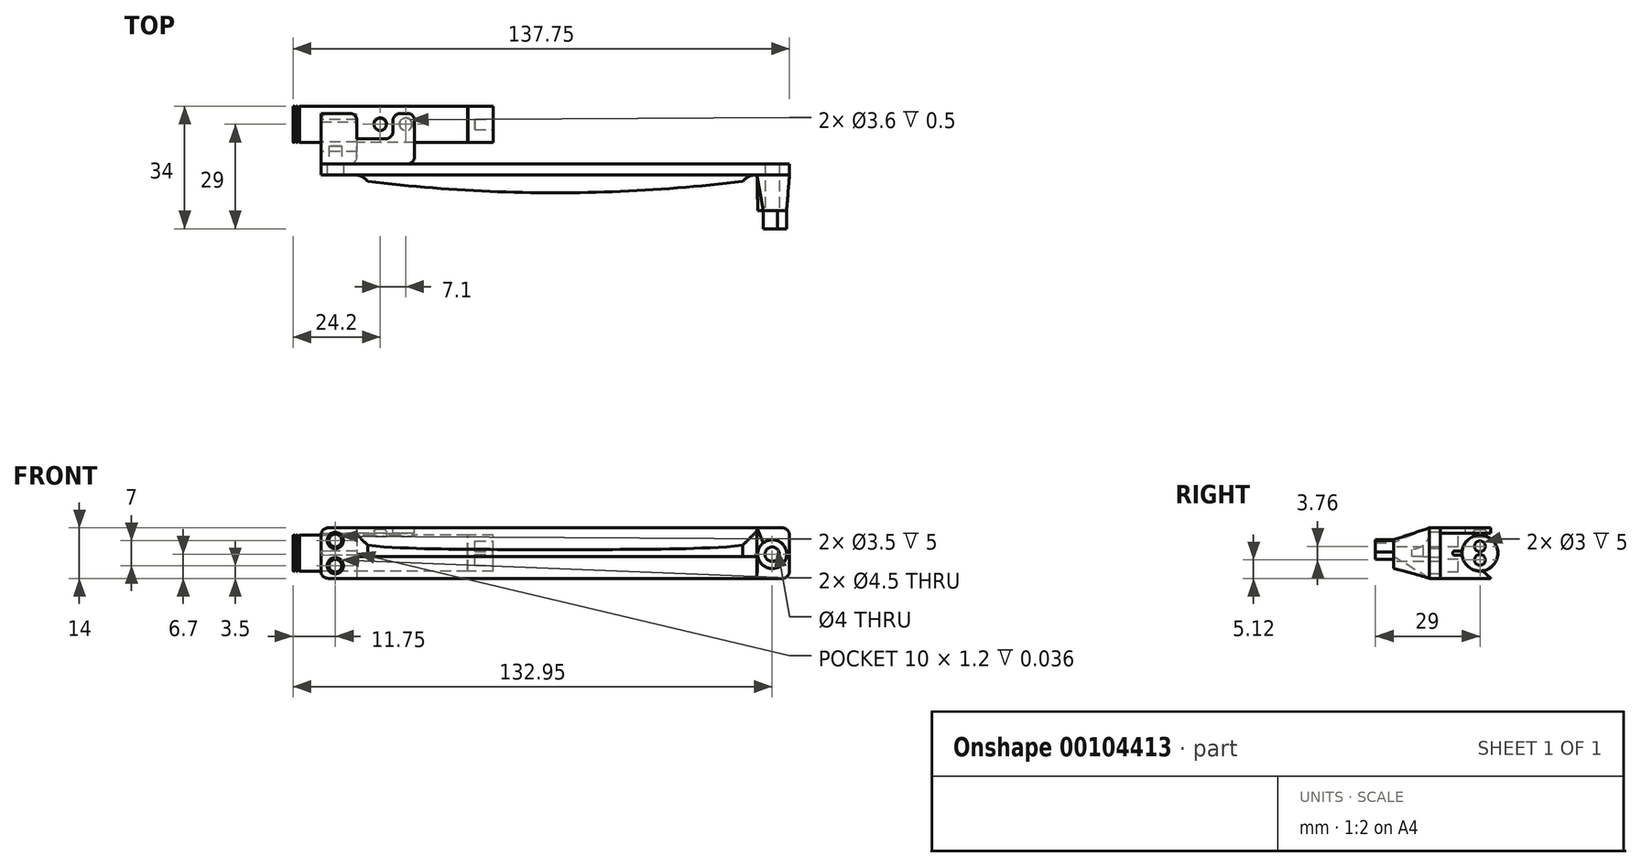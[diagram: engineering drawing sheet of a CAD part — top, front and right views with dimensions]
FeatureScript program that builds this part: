
annotation { "Feature Type Name" : "Feature", "Feature Type Description" : "" }
export const myFeature = defineFeature(function(context is Context, id is Id, definition is map)
    precondition{}
    {
        {
            var Q0;
            Q0=qCreatedBy(makeId("Right.planeOp"),FACE);
            var sketch = newSketch(context, id + "F0", { "sketchPlane" : qUnion([Q0])});
            skCircle(sketch, "E0", {"center": v(0, 0) * mm, "radius": 5 * mm});
            skSolve(sketch);
        }
        {
            var Q0;
            Q0 = qSketchRegion(id + "F0", true);
            extrude(context, id + "F1", {"entities" : qUnion([Q0]), "endBound" : BoundingType.SYMMETRIC, "depth" : 55.5 * mm});
        }
        {
            var Q0;
            Q0=makeQuery(id+"F1.opExtrude","CAP_FACE",FACE,{"disambiguationData":[OSD([sQuery(id+"F0.wireOp",EDGE,"E0")])],"isStart":false});
            var sketch = newSketch(context, id + "F2", { "sketchPlane" : qUnion([Q0])});
            skPoint(sketch, "E1", {"position": v(0, 5) * mm});
            skLineSegment(sketch, "E2", {"start": v(0, 0) * mm, "end": v(0, 5) * mm});
            skSolve(sketch);
        }
        {
            var Q0;
            Q0=qCreatedBy(makeId("Front.planeOp"),FACE);
            var sketch = newSketch(context, id + "F3", { "sketchPlane" : qUnion([Q0])});
            skLineSegment(sketch, "E3.bottom", {"start": v(20.65, 5) * mm, "end": v(20.75, 5) * mm});
            skLineSegment(sketch, "E3.top", {"start": v(20.65, 4.8) * mm, "end": v(20.75, 4.8) * mm});
            skLineSegment(sketch, "E3.left", {"start": v(20.65, 5) * mm, "end": v(20.65, 4.8) * mm});
            skLineSegment(sketch, "E3.right", {"start": v(20.75, 5) * mm, "end": v(20.75, 4.8) * mm});
            skSolve(sketch);
        }
        {
            var Q0;
            Q0 = qSketchRegion(id + "F3", true);
            var Q1;
            Q1=makeQuery(id+"F1.opExtrude","CAP_EDGE",EDGE,{"disambiguationData":[OSD([sQuery(id+"F0.wireOp",EDGE,"E0")])],"isStart":false});
            revolve(context, id + "F4", {"operationType" : NewBodyOperationType.REMOVE, "entities" : qUnion([Q0]), "axis" : qUnion([Q1]), "revolveType" : RevolveType.FULL, "oppositeDirection" : true});
        }
        {
            var Q0;
            Q0=qCreatedBy(makeId("Front.planeOp"),FACE);
            var sketch = newSketch(context, id + "F5", { "sketchPlane" : qUnion([Q0])});
            skArc(sketch, "E4", {"start": v(-26.42, 4.88) * mm, "mid": v(-26.14, 4.76) * mm, "end": v(-25.95, 5) * mm});
            skArc(sketch, "E5", {"start": v(-27.32, 5) * mm, "mid": v(-27.32, 5) * mm, "end": v(-27.32, 5) * mm});
            skArc(sketch, "E6", {"start": v(-26.38, 4.74) * mm, "mid": v(-26.38, 4.75) * mm, "end": v(-26.38, 4.75) * mm});
            skLineSegment(sketch, "E7", {"start": v(-27.07, 5) * mm, "end": v(-26.2, 5) * mm, "construction": true});
            skLineSegment(sketch, "E8", {"start": v(-26.87, 4.66) * mm, "end": v(-26.4, 4.66) * mm, "construction": true});
            skLineSegment(sketch, "E9", {"start": v(-27.07, 5) * mm, "end": v(-27.07, 5.56) * mm, "construction": true});
            skArc(sketch, "E10.MirrorCS", {"start": v(-27.75, 4.75) * mm, "mid": v(-27.56, 5) * mm, "end": v(-27.28, 4.87) * mm});
            skLineSegment(sketch, "E11.MirrorCS", {"start": v(-27.75, 4.75) * mm, "end": v(-27.75, 5) * mm});
            skPoint(sketch, "E12.orphan", {"position": v(-27.25, 5.35) * mm});
            skPoint(sketch, "E13.orphan", {"position": v(-26.88, 5.35) * mm});
            skPoint(sketch, "E14.orphan", {"position": v(-26.38, 5.32) * mm});
            skPoint(sketch, "E15.orphan", {"position": v(-27.25, 4.6) * mm});
            skPoint(sketch, "E16.orphan", {"position": v(-27.27, 4.66) * mm});
            skPoint(sketch, "E17.orphan", {"position": v(-27.73, 4.66) * mm});
            skPoint(sketch, "E18.orphan", {"position": v(-26.88, 4.6) * mm});
            skLineSegment(sketch, "E19", {"start": v(-25.95, 5.27) * mm, "end": v(-25.95, 4.5) * mm, "construction": true});
            skLineSegment(sketch, "E20", {"start": v(-25.95, 5) * mm, "end": v(-26.45, 5) * mm});
            skLineSegment(sketch, "E21", {"start": v(-26.45, 5) * mm, "end": v(-27.75, 5) * mm});
            skPoint(sketch, "E22.orphan", {"position": v(-27.75, 5.32) * mm});
            skPoint(sketch, "E23.orphan", {"position": v(-26.38, 4.67) * mm});
            skArc(sketch, "E24.trimOffspring", {"start": v(-27.28, 4.87) * mm, "mid": v(-27.07, 4.75) * mm, "end": v(-26.85, 4.87) * mm});
            skArc(sketch, "E25.trimOffspring", {"start": v(-27.25, 4.75) * mm, "mid": v(-27.25, 4.75) * mm, "end": v(-27.25, 4.74) * mm});
            skArc(sketch, "E26.trimOffspring", {"start": v(-26.88, 4.75) * mm, "mid": v(-26.88, 4.75) * mm, "end": v(-26.88, 4.74) * mm});
            skArc(sketch, "E27.trimOffspring", {"start": v(-26.42, 4.88) * mm, "mid": v(-26.63, 5) * mm, "end": v(-26.85, 4.87) * mm});
            skPoint(sketch, "E28.orphan", {"position": v(-27.75, 4.67) * mm});
            skSolve(sketch);
        }
        {
            var Q0;
            Q0 = qSketchRegion(id + "F5", true);
            var Q1;
            {var subQ0=sQuery(id+"F0.wireOp",EDGE,"E0");Q1=makeQuery(id+"F4.boolean.opBoolean","SPLIT",FACE,{"disambiguationData":[TD([makeQuery(id+"F1.opExtrude","CAP_FACE",FACE,{"disambiguationData":[OSD([subQ0])],"isStart":true})])],"derivedFrom":makeQuery(id+"F1.opExtrude","SWEPT_FACE",FACE,{"disambiguationData":[OSD([subQ0])]})});}
            revolve(context, id + "F6", {"operationType" : NewBodyOperationType.REMOVE, "entities" : qUnion([Q0]), "axis" : qUnion([Q1]), "revolveType" : RevolveType.FULL, "oppositeDirection" : true});
        }
        {
            var Q0;
            Q0=makeQuery(id+"F1.opExtrude","CAP_FACE",FACE,{"disambiguationData":[OSD([sQuery(id+"F0.wireOp",EDGE,"E0")])],"isStart":false});
            var sketch = newSketch(context, id + "F7", { "sketchPlane" : qUnion([Q0])});
            skCircle(sketch, "E29", {"center": v(0, 1.88) * mm, "radius": 1.5 * mm});
            skCircle(sketch, "E30", {"center": v(0, -1.88) * mm, "radius": 1.5 * mm});
            skLineSegment(sketch, "E31", {"start": v(0, 1.88) * mm, "end": v(0, 0) * mm, "construction": true});
            skLineSegment(sketch, "E32", {"start": v(0, 0) * mm, "end": v(0, -1.88) * mm, "construction": true});
            skSolve(sketch);
        }
        {
            var Q0;
            Q0 = qSketchRegion(id + "F7", true);
            extrude(context, id + "F8", {"entities" : qUnion([Q0]), "operationType" : NewBodyOperationType.REMOVE, "oppositeDirection" : true, "depth" : 5 * mm});
        }
        {
            var Q0;
            Q0=sQuery(id+"F2.wireOp",VERTEX,"E1");
            var Q1;
            Q1=qCreatedBy(makeId("Top.planeOp"),FACE);
            cPlane(context, id + "F9", {"entities" : qUnion([Q0, Q1]), "cplaneType" : CPlaneType.PLANE_POINT, "offset" : 150 * mm, "width" : 150 * mm, "height" : 150 * mm});
        }
        {
            var Q0;
            Q0=qCreatedBy(id+"F9.planeOp",FACE);
            var sketch = newSketch(context, id + "F10", { "sketchPlane" : qUnion([Q0])});
            skCircle(sketch, "E33", {"center": v(-3.55, 0) * mm, "radius": 1.7 * mm});
            skCircle(sketch, "E34", {"center": v(3.55, 0) * mm, "radius": 1.7 * mm});
            skSolve(sketch);
        }
        {
            var Q0;
            Q0 = qSketchRegion(id + "F10", true);
            var Q1;
            {var subQ0=sQuery(id+"F0.wireOp",EDGE,"E0");Q1=makeQuery(id+"F4.boolean.opBoolean","SPLIT",FACE,{"disambiguationData":[TD([makeQuery(id+"F1.opExtrude","CAP_FACE",FACE,{"disambiguationData":[OSD([subQ0])],"isStart":true})])],"derivedFrom":makeQuery(id+"F1.opExtrude","SWEPT_FACE",FACE,{"disambiguationData":[OSD([subQ0])]})});}
            extrude(context, id + "F11", {"entities" : qUnion([Q0]), "operationType" : NewBodyOperationType.ADD, "depth" : 1.5 * mm, "hasSecondDirection" : true, "secondDirectionBound" : SecondDirectionBoundingType.UP_TO_SURFACE, "secondDirectionOppositeDirection" : true, "secondDirectionBoundEntityFace" : qUnion([Q1]), "secondDirectionDepth" : 25 * mm});
        }
        {
            var Q0;
            Q0=makeQuery(id+"F11.opExtrude","CAP_EDGE",EDGE,{"disambiguationData":[OSD([sQuery(id+"F10.wireOp",EDGE,"E33")]),OD(1.0)],"isStart":false});
            var Q1;
            Q1=makeQuery(id+"F11.opExtrude","CAP_EDGE",EDGE,{"disambiguationData":[OSD([sQuery(id+"F10.wireOp",EDGE,"E34")]),OD(1.0)],"isStart":false});
            fillet(context, id + "F12", {"entities" : qUnion([Q0, Q1]), "radius" : .5 * mm, "tangentPropagation" : true, "allowEdgeOverflow" : false});
        }
        {
            var Q0;
            Q0=qCreatedBy(id+"F9.planeOp",FACE);
            var sketch = newSketch(context, id + "F13", { "sketchPlane" : qUnion([Q0])});
            skCircle(sketch, "E35.0", {"center": v(-3.55, 0) * mm, "radius": 1.7 * mm});
            skCircle(sketch, "E35.1", {"center": v(3.55, 0) * mm, "radius": 1.7 * mm});
            skCircle(sketch, "E36.0", {"center": v(-3.55, 0) * mm, "radius": 1.8 * mm});
            skCircle(sketch, "E37.0", {"center": v(3.55, 0) * mm, "radius": 1.8 * mm});
            skSolve(sketch);
        }
        {
            var Q0;
            Q0 = qSketchRegion(id + "F13", true);
            extrude(context, id + "F14", {"entities" : qUnion([Q0]), "operationType" : NewBodyOperationType.REMOVE, "oppositeDirection" : true, "depth" : .5 * mm});
        }
        {
            var Q0;
            Q0=qCreatedBy(makeId("Right.planeOp"),FACE);
            cPlane(context, id + "F15", {"entities" : qUnion([Q0]), "cplaneType" : CPlaneType.OFFSET, "offset" : 10 * mm, "oppositeDirection" : true, "width" : 150 * mm, "height" : 150 * mm});
        }
        {
            var Q0;
            Q0=qCreatedBy(id+"F15.planeOp",FACE);
            var sketch = newSketch(context, id + "F16", { "sketchPlane" : qUnion([Q0])});
            skArc(sketch, "E38.0", {"start": v(3, 4) * mm, "mid": v(-5, 0) * mm, "end": v(3, -4) * mm});
            skLineSegment(sketch, "E39", {"start": v(3, 7) * mm, "end": v(3, 4) * mm});
            skLineSegment(sketch, "E40", {"start": v(0, 0) * mm, "end": v(3, 0) * mm});
            skLineSegment(sketch, "E41", {"start": v(3, 7) * mm, "end": v(-11, 7) * mm});
            skLineSegment(sketch, "E42", {"start": v(-11, 7) * mm, "end": v(-11, -7) * mm});
            skLineSegment(sketch, "E43", {"start": v(-11, -7) * mm, "end": v(3, -7) * mm});
            skLineSegment(sketch, "E44.trimOffspring", {"start": v(3, -4) * mm, "end": v(3, -7) * mm});
            skSolve(sketch);
        }
        {
            var Q0;
            Q0 = qSketchRegion(id + "F16", true);
            extrude(context, id + "F17", {"entities" : qUnion([Q0]), "oppositeDirection" : true, "depth" : 10 * mm});
        }
        {
            var Q0;
            Q0=makeQuery(id+"F17.opExtrude","SWEPT_EDGE",EDGE,{"disambiguationData":[OSD([sQuery(id+"F16.wireOp",EDGE,"E38.0"),sQuery(id+"F16.wireOp",EDGE,"E39")])]});
            var Q1;
            Q1=makeQuery(id+"F17.opExtrude","SWEPT_EDGE",EDGE,{"disambiguationData":[OSD([sQuery(id+"F16.wireOp",EDGE,"E38.0"),sQuery(id+"F16.wireOp",EDGE,"E44.trimOffspring")])]});
            chamfer(context, id + "F18", {"entities" : qUnion([Q0, Q1]), "width" : 2 * mm, "tangentPropagation" : true});
        }
        {
            var Q0;
            Q0=makeQuery(id+"F17.opExtrude","SWEPT_FACE",FACE,{"disambiguationData":[OSD([sQuery(id+"F16.wireOp",EDGE,"E41")])]});
            var sketch = newSketch(context, id + "F19", { "sketchPlane" : qUnion([Q0])});
            skLineSegment(sketch, "E45.bottom", {"start": v(0, 3) * mm, "end": v(6, 3) * mm});
            skLineSegment(sketch, "E45.top", {"start": v(-20, -11) * mm, "end": v(6, -11) * mm});
            skLineSegment(sketch, "E45.left", {"start": v(-20, 3) * mm, "end": v(-20, -11) * mm});
            skLineSegment(sketch, "E45.right", {"start": v(6, 3) * mm, "end": v(6, -11) * mm});
            skLineSegment(sketch, "E46", {"start": v(0, 3) * mm, "end": v(0, -4) * mm});
            skLineSegment(sketch, "E47", {"start": v(0, -4) * mm, "end": v(-10, -4) * mm});
            skLineSegment(sketch, "E48", {"start": v(-10, -4) * mm, "end": v(-10, 3) * mm});
            skLineSegment(sketch, "E49", {"start": v(-10, 3) * mm, "end": v(-20, 3) * mm});
            skSolve(sketch);
        }
        {
            var Q0;
            Q0 = qSketchRegion(id + "F19", true);
            extrude(context, id + "F20", {"entities" : qUnion([Q0]), "operationType" : NewBodyOperationType.ADD, "oppositeDirection" : true, "depth" : 1.5 * mm});
        }
        {
            var Q0;
            Q0=makeQuery(id+"F20.opExtrude","SWEPT_EDGE",EDGE,{"disambiguationData":[OSD([sQuery(id+"F19.wireOp",EDGE,"E46"),sQuery(id+"F19.wireOp",EDGE,"E47")])]});
            var Q1;
            Q1=makeQuery(id+"F20.opExtrude","SWEPT_EDGE",EDGE,{"disambiguationData":[OSD([sQuery(id+"F16.wireOp",EDGE,"E41"),sQuery(id+"F19.wireOp",EDGE,"E47"),sQuery(id+"F19.wireOp",EDGE,"E48")])]});
            var Q2;
            Q2=makeQuery(id+"F20.boolean.opBoolean","MERGE",EDGE,{"derivedFrom":[makeQuery(id+"F17.opExtrude","CAP_EDGE",EDGE,{"disambiguationData":[OSD([sQuery(id+"F16.wireOp",EDGE,"E39")])],"isStart":true}),makeQuery(id+"F20.opExtrude","SWEPT_EDGE",EDGE,{"disambiguationData":[OSD([sQuery(id+"F19.wireOp",EDGE,"E48"),sQuery(id+"F19.wireOp",EDGE,"E49")])]})]});
            var Q3;
            Q3=makeQuery(id+"F20.opExtrude","SWEPT_EDGE",EDGE,{"disambiguationData":[OSD([sQuery(id+"F19.wireOp",EDGE,"E45.bottom"),sQuery(id+"F19.wireOp",EDGE,"E46")])]});
            var Q4;
            Q4=makeQuery(id+"F17.opExtrude","CAP_EDGE",EDGE,{"disambiguationData":[OSD([sQuery(id+"F16.wireOp",EDGE,"E42")])],"isStart":true});
            var Q5;
            Q5=makeQuery(id+"F20.opExtrude","SWEPT_EDGE",EDGE,{"disambiguationData":[OSD([sQuery(id+"F19.wireOp",EDGE,"E45.top"),sQuery(id+"F19.wireOp",EDGE,"E45.right")])]});
            var Q6;
            Q6=makeQuery(id+"F20.opExtrude","SWEPT_EDGE",EDGE,{"disambiguationData":[OSD([sQuery(id+"F19.wireOp",EDGE,"E45.bottom"),sQuery(id+"F19.wireOp",EDGE,"E45.right")])]});
            fillet(context, id + "F21", {"entities" : qUnion([Q0, Q1, Q2, Q3, Q4, Q5, Q6]), "radius" : 2 * mm, "tangentPropagation" : true, "allowEdgeOverflow" : false});
        }
        {
            var Q0;
            Q0=makeQuery(id+"F20.boolean.opBoolean","MERGE",FACE,{"derivedFrom":[makeQuery(id+"F17.opExtrude","CAP_FACE",FACE,{"disambiguationData":[OSD([sQuery(id+"F16.wireOp",EDGE,"E38.0"),sQuery(id+"F16.wireOp",EDGE,"E39"),sQuery(id+"F16.wireOp",EDGE,"E41"),sQuery(id+"F16.wireOp",EDGE,"E42"),sQuery(id+"F16.wireOp",EDGE,"E43"),sQuery(id+"F16.wireOp",EDGE,"E44.trimOffspring")])],"isStart":false}),makeQuery(id+"F20.opExtrude","SWEPT_FACE",FACE,{"disambiguationData":[OSD([sQuery(id+"F19.wireOp",EDGE,"E45.left")])]})]});
            var sketch = newSketch(context, id + "F22", { "sketchPlane" : qUnion([Q0])});
            skLineSegment(sketch, "E50", {"start": v(6.96, 0.6) * mm, "end": v(4.96, 0.6) * mm});
            skLineSegment(sketch, "E51", {"start": v(4.96, 0.6) * mm, "end": v(4.96, -0.6) * mm});
            skLineSegment(sketch, "E52", {"start": v(4.96, -0.6) * mm, "end": v(6.96, -0.6) * mm});
            skLineSegment(sketch, "E53", {"start": v(0, 0) * mm, "end": v(9, 0) * mm, "construction": true});
            skArc(sketch, "E54", {"start": v(6.96, -0.6) * mm, "mid": v(7.56, 0) * mm, "end": v(6.96, 0.6) * mm});
            skSolve(sketch);
        }
        {
            var Q0;
            {var subQ0=sQuery(id+"F22.wireOp",EDGE,"yF9MeYyX-MxWM-4ZoS-nlc9-Eh6hePXLtj0A");Q0=makeQuery(id+"F22.imprint","IMPRINT",FACE,{"disambiguationData":[TD([[makeQuery(id+"F22.imprint","IMPRINT",EDGE,{"derivedFrom":subQ0}),1.0]])]});}
            var Q1;
            {var subQ0=sQuery(id+"F22.wireOp",EDGE,"E50");Q1=makeQuery(id+"F22.imprint","IMPRINT",FACE,{"disambiguationData":[TD([[makeQuery(id+"F22.imprint","IMPRINT",EDGE,{"derivedFrom":subQ0}),1.0]])]});}
            var Q2;
            Q2=makeQuery(id+"F20.boolean.opBoolean","MERGE",FACE,{"derivedFrom":[makeQuery(id+"F17.opExtrude","CAP_FACE",FACE,{"disambiguationData":[OSD([sQuery(id+"F16.wireOp",EDGE,"E38.0"),sQuery(id+"F16.wireOp",EDGE,"E39"),sQuery(id+"F16.wireOp",EDGE,"E41"),sQuery(id+"F16.wireOp",EDGE,"E42"),sQuery(id+"F16.wireOp",EDGE,"E43"),sQuery(id+"F16.wireOp",EDGE,"E44.trimOffspring")])],"isStart":true}),makeQuery(id+"F20.opExtrude","SWEPT_FACE",FACE,{"disambiguationData":[OSD([sQuery(id+"F19.wireOp",EDGE,"E48")])]})]});
            extrude(context, id + "F23", {"entities" : qUnion([Q0, Q1]), "operationType" : NewBodyOperationType.REMOVE, "endBound" : BoundingType.UP_TO_SURFACE, "oppositeDirection" : true, "endBoundEntityFace" : qUnion([Q2]), "depth" : 25 * mm});
        }
        {
            var Q0;
            Q0=makeQuery(id+"F20.boolean.opBoolean","MERGE",FACE,{"derivedFrom":[makeQuery(id+"F17.opExtrude","SWEPT_FACE",FACE,{"disambiguationData":[OSD([sQuery(id+"F16.wireOp",EDGE,"E42")])]}),makeQuery(id+"F20.opExtrude","SWEPT_FACE",FACE,{"disambiguationData":[OSD([sQuery(id+"F19.wireOp",EDGE,"E45.top")])]})]});
            var sketch = newSketch(context, id + "F24", { "sketchPlane" : qUnion([Q0])});
            skCircle(sketch, "E55", {"center": v(-16, 3.5) * mm, "radius": 1.75 * mm});
            skCircle(sketch, "E56", {"center": v(-16, -3.5) * mm, "radius": 1.75 * mm});
            skLineSegment(sketch, "E57", {"start": v(-16, 3.5) * mm, "end": v(-16, -3.5) * mm, "construction": true});
            skLineSegment(sketch, "E58", {"start": v(0, 0) * mm, "end": v(-16, 0) * mm, "construction": true});
            skLineSegment(sketch, "E59", {"start": v(-16, -7) * mm, "end": v(-16, -3.5) * mm, "construction": true});
            skSolve(sketch);
        }
        {
            var Q0;
            Q0 = qSketchRegion(id + "F24", true);
            extrude(context, id + "F25", {"entities" : qUnion([Q0]), "operationType" : NewBodyOperationType.REMOVE, "oppositeDirection" : true, "depth" : 5 * mm});
        }
        {
            var Q0;
            Q0=makeQuery(id+"F20.boolean.opBoolean","MERGE",FACE,{"derivedFrom":[makeQuery(id+"F17.opExtrude","SWEPT_FACE",FACE,{"disambiguationData":[OSD([sQuery(id+"F16.wireOp",EDGE,"E42")])]}),makeQuery(id+"F20.opExtrude","SWEPT_FACE",FACE,{"disambiguationData":[OSD([sQuery(id+"F19.wireOp",EDGE,"E45.top")])]})]});
            var sketch = newSketch(context, id + "F26", { "sketchPlane" : qUnion([Q0])});
            skLineSegment(sketch, "E60.bottom", {"start": v(-20, 7) * mm, "end": v(110, 7) * mm});
            skLineSegment(sketch, "E60.top", {"start": v(-20, -7) * mm, "end": v(110, -7) * mm});
            skLineSegment(sketch, "E60.left", {"start": v(-20, 7) * mm, "end": v(-20, -7) * mm});
            skLineSegment(sketch, "E60.right", {"start": v(110, 7) * mm, "end": v(110, -7) * mm});
            skSolve(sketch);
        }
        {
            var Q0;
            Q0 = qSketchRegion(id + "F26", true);
            extrude(context, id + "F27", {"entities" : qUnion([Q0]), "depth" : 3 * mm});
        }
        {
            var Q0;
            Q0=makeQuery(id+"F27.opExtrude","CAP_FACE",FACE,{"disambiguationData":[OSD([sQuery(id+"F26.wireOp",EDGE,"E60.bottom"),sQuery(id+"F26.wireOp",EDGE,"E60.top"),sQuery(id+"F26.wireOp",EDGE,"E60.left"),sQuery(id+"F26.wireOp",EDGE,"E60.right")])],"isStart":false});
            var sketch = newSketch(context, id + "F28", { "sketchPlane" : qUnion([Q0])});
            skPoint(sketch, "E61", {"position": v(-20, 0) * mm});
            skSolve(sketch);
        }
        {
            var Q0;
            Q0=sQuery(id+"F28.wireOp",VERTEX,"E61");
            var Q1;
            Q1=qCreatedBy(makeId("Top.planeOp"),FACE);
            cPlane(context, id + "F29", {"entities" : qUnion([Q0, Q1]), "cplaneType" : CPlaneType.PLANE_POINT, "offset" : 150 * mm, "width" : 150 * mm, "height" : 150 * mm});
        }
        {
            var Q0;
            Q0=qCreatedBy(id+"F29.planeOp",FACE);
            var sketch = newSketch(context, id + "F30", { "sketchPlane" : qUnion([Q0])});
            skArc(sketch, "E62", {"start": v(-20, -14) * mm, "mid": v(45, -19) * mm, "end": v(110, -14) * mm});
            skLineSegment(sketch, "E63", {"start": v(-20, -14) * mm, "end": v(110, -14) * mm});
            skSolve(sketch);
        }
        {
            var Q0;
            Q0 = qSketchRegion(id + "F30", true);
            extrude(context, id + "F31", {"entities" : qUnion([Q0]), "operationType" : NewBodyOperationType.ADD, "endBound" : BoundingType.SYMMETRIC, "depth" : 2 * mm});
        }
        {
            var Q0;
            Q0=makeQuery(id+"F28.imprint","IMPRINT",FACE,{"disambiguationData":[TD([[makeQuery(id+"F28.imprint","IMPRINT",EDGE,{"derivedFrom":makeQuery(id+"F27.opExtrude","CAP_EDGE",EDGE,{"disambiguationData":[OSD([sQuery(id+"F26.wireOp",EDGE,"E60.bottom")])],"isStart":false})}),-1.0]])]});
            var sketch = newSketch(context, id + "F32", { "sketchPlane" : qUnion([Q0])});
            skPoint(sketch, "E64", {"position": v(-16, 3.5) * mm});
            skPoint(sketch, "E65", {"position": v(-16, -3.5) * mm});
            skSolve(sketch);
        }
        {
            var Q0;
            Q0=sQuery(id+"F32.wireOp",VERTEX,"E64");
            var Q1;
            Q1=sQuery(id+"F32.wireOp",VERTEX,"E65");
            var Q2;
            Q2=makeQuery(id+"F27.opExtrude","SWEPT_BODY",BODY,{"disambiguationData":[OSD([sQuery(id+"F26.wireOp",EDGE,"E60.bottom"),sQuery(id+"F26.wireOp",EDGE,"E60.top"),sQuery(id+"F26.wireOp",EDGE,"E60.left"),sQuery(id+"F26.wireOp",EDGE,"E60.right")])]});
            hole(context, id + "F33", {"style" : HoleStyle.SIMPLE, "endStyle" : HoleEndStyle.THROUGH, "holeDiameter" : 4.5 * mm, "locations" : qUnion([Q0, Q1]), "scope" : qUnion([Q2]), "isTappedThrough" : true});
        }
        {
            var Q0;
            Q0=makeQuery(id+"F28.imprint","IMPRINT",FACE,{"disambiguationData":[TD([[makeQuery(id+"F28.imprint","IMPRINT",EDGE,{"derivedFrom":makeQuery(id+"F27.opExtrude","CAP_EDGE",EDGE,{"disambiguationData":[OSD([sQuery(id+"F26.wireOp",EDGE,"E60.bottom")])],"isStart":false})}),-1.0]])]});
            var sketch = newSketch(context, id + "F34", { "sketchPlane" : qUnion([Q0])});
            skPoint(sketch, "E66", {"position": v(45, -7) * mm});
            skSolve(sketch);
        }
        {
            var Q0;
            Q0=qCreatedBy(makeId("Right.planeOp"),FACE);
            var Q1;
            Q1=sQuery(id+"F34.wireOp",VERTEX,"E66");
            cPlane(context, id + "F35", {"entities" : qUnion([Q0, Q1]), "cplaneType" : CPlaneType.PLANE_POINT, "offset" : 150 * mm, "width" : 150 * mm, "height" : 150 * mm});
        }
        {
            var Q0;
            Q0=makeQuery(id+"F31.opExtrude","CAP_FACE",FACE,{"disambiguationData":[OSD([sQuery(id+"F30.wireOp",EDGE,"E62"),sQuery(id+"F30.wireOp",EDGE,"E63")])],"isStart":true});
            var sketch = newSketch(context, id + "F36", { "sketchPlane" : qUnion([Q0])});
            skLineSegment(sketch, "E67.bottom", {"start": v(-20, 19) * mm, "end": v(-7, 19) * mm});
            skLineSegment(sketch, "E67.top", {"start": v(-20, 14) * mm, "end": v(-7, 14) * mm});
            skLineSegment(sketch, "E67.left", {"start": v(-20, 19) * mm, "end": v(-20, 14) * mm});
            skLineSegment(sketch, "E67.right", {"start": v(-7, 19) * mm, "end": v(-7, 14) * mm});
            skLineSegment(sketch, "E68.MirrorCS", {"start": v(110, 19) * mm, "end": v(110, 14) * mm});
            skLineSegment(sketch, "E69.MirrorCS", {"start": v(97, 19) * mm, "end": v(97, 14) * mm});
            skLineSegment(sketch, "E70.MirrorCS", {"start": v(110, 19) * mm, "end": v(97, 19) * mm});
            skLineSegment(sketch, "E71.MirrorCS", {"start": v(110, 14) * mm, "end": v(97, 14) * mm});
            skSolve(sketch);
        }
        {
            var Q0;
            {var subQ0=sQuery(id+"F36.wireOp",EDGE,"E67.top");Q0=makeQuery(id+"F36.imprint","IMPRINT",FACE,{"disambiguationData":[TD([[makeQuery(id+"F36.imprint","IMPRINT",EDGE,{"derivedFrom":subQ0}),1.0]])]});}
            var Q1;
            {var subQ0=sQuery(id+"F36.wireOp",EDGE,"E71.MirrorCS");Q1=makeQuery(id+"F36.imprint","IMPRINT",FACE,{"disambiguationData":[TD([[makeQuery(id+"F36.imprint","IMPRINT",EDGE,{"derivedFrom":subQ0}),1.0]])]});}
            extrude(context, id + "F37", {"entities" : qUnion([Q0, Q1]), "operationType" : NewBodyOperationType.REMOVE, "endBound" : BoundingType.THROUGH_ALL, "oppositeDirection" : true, "depth" : 25 * mm});
        }
        {
            var Q0;
            Q0=makeQuery(id+"F27.opExtrude","SWEPT_EDGE",EDGE,{"disambiguationData":[OSD([sQuery(id+"F26.wireOp",EDGE,"E60.bottom"),sQuery(id+"F26.wireOp",EDGE,"E60.left")])]});
            var Q1;
            Q1=makeQuery(id+"F17.opExtrude","CAP_EDGE",EDGE,{"disambiguationData":[OSD([sQuery(id+"F16.wireOp",EDGE,"E41")])],"isStart":false});
            var Q2;
            Q2=makeQuery(id+"F17.opExtrude","CAP_EDGE",EDGE,{"disambiguationData":[OSD([sQuery(id+"F16.wireOp",EDGE,"E43")])],"isStart":false});
            var Q3;
            Q3=makeQuery(id+"F27.opExtrude","SWEPT_EDGE",EDGE,{"disambiguationData":[OSD([sQuery(id+"F26.wireOp",EDGE,"E60.top"),sQuery(id+"F26.wireOp",EDGE,"E60.left")])]});
            var Q4;
            Q4=makeQuery(id+"F27.opExtrude","SWEPT_EDGE",EDGE,{"disambiguationData":[OSD([sQuery(id+"F26.wireOp",EDGE,"E60.bottom"),sQuery(id+"F26.wireOp",EDGE,"E60.right")])]});
            var Q5;
            Q5=makeQuery(id+"F27.opExtrude","SWEPT_EDGE",EDGE,{"disambiguationData":[OSD([sQuery(id+"F26.wireOp",EDGE,"E60.top"),sQuery(id+"F26.wireOp",EDGE,"E60.right")])]});
            var Q6;
            Q6=makeQuery(id+"F37.boolean.opBoolean","COPY",EDGE,{"derivedFrom":makeQuery(id+"F37.opExtrude","SWEPT_EDGE",EDGE,{"disambiguationData":[OSD([sQuery(id+"F30.wireOp",EDGE,"E62"),sQuery(id+"F36.wireOp",EDGE,"E69.MirrorCS")])]})});
            var Q7;
            Q7=makeQuery(id+"F37.boolean.opBoolean","COPY",EDGE,{"derivedFrom":makeQuery(id+"F37.opExtrude","SWEPT_EDGE",EDGE,{"disambiguationData":[OSD([sQuery(id+"F30.wireOp",EDGE,"E62"),sQuery(id+"F36.wireOp",EDGE,"E67.right")])]})});
            fillet(context, id + "F38", {"entities" : qUnion([Q0, Q1, Q2, Q3, Q4, Q5, Q6, Q7]), "radius" : 2 * mm, "tangentPropagation" : true, "allowEdgeOverflow" : false});
        }
        {
            var Q0;
            Q0=makeQuery(id+"F31.opExtrude","CAP_EDGE",EDGE,{"disambiguationData":[OSD([sQuery(id+"F30.wireOp",EDGE,"E63")])],"isStart":true});
            var Q1;
            Q1=makeQuery(id+"F31.opExtrude","CAP_EDGE",EDGE,{"disambiguationData":[OSD([sQuery(id+"F30.wireOp",EDGE,"E63")])],"isStart":false});
            var Q2;
            Q2=makeQuery(id+"F37.boolean.opBoolean","COPY",EDGE,{"derivedFrom":makeQuery(id+"F37.opExtrude","SWEPT_EDGE",EDGE,{"disambiguationData":[OSD([sQuery(id+"F30.wireOp",EDGE,"E63"),sQuery(id+"F36.wireOp",EDGE,"E69.MirrorCS"),sQuery(id+"F36.wireOp",EDGE,"E71.MirrorCS")])]})});
            var Q3;
            Q3=makeQuery(id+"F37.boolean.opBoolean","COPY",EDGE,{"derivedFrom":makeQuery(id+"F37.opExtrude","SWEPT_EDGE",EDGE,{"disambiguationData":[OSD([sQuery(id+"F30.wireOp",EDGE,"E63"),sQuery(id+"F36.wireOp",EDGE,"E67.top"),sQuery(id+"F36.wireOp",EDGE,"E67.right")])]})});
            fillet(context, id + "F39", {"entities" : qUnion([Q0, Q1, Q2, Q3]), "radius" : 5 * mm, "tangentPropagation" : true, "allowEdgeOverflow" : false});
        }
        {
            var Q0;
            {var subQ2=sQuery(id+"F26.wireOp",EDGE,"E60.top");var subQ3=sQuery(id+"F26.wireOp",EDGE,"E60.right");var subQ5=sQuery(id+"F26.wireOp",EDGE,"E60.left");var subQ8=sQuery(id+"F26.wireOp",EDGE,"E60.bottom");var subQ9=makeQuery(id+"F27.opExtrude","CAP_FACE",FACE,{"disambiguationData":[OSD([subQ8,subQ2,subQ5,subQ3])],"isStart":false});Q0=makeQuery(id+"F37.boolean.opBoolean","MERGE",FACE,{"derivedFrom":[makeQuery(id+"F31.boolean.opBoolean","SPLIT",FACE,{"disambiguationData":[TD([makeQuery(id+"F27.opExtrude","SWEPT_FACE",FACE,{"disambiguationData":[OSD([subQ8])]})])],"derivedFrom":subQ9}),makeQuery(id+"F31.boolean.opBoolean","SPLIT",FACE,{"disambiguationData":[TD([makeQuery(id+"F27.opExtrude","SWEPT_FACE",FACE,{"disambiguationData":[OSD([subQ2])]})])],"derivedFrom":subQ9}),makeQuery(id+"F37.opExtrude","SWEPT_FACE",FACE,{"disambiguationData":[OSD([sQuery(id+"F36.wireOp",EDGE,"E67.top")])]}),makeQuery(id+"F37.opExtrude","SWEPT_FACE",FACE,{"disambiguationData":[OSD([sQuery(id+"F36.wireOp",EDGE,"E71.MirrorCS")])]})]});}
            var sketch = newSketch(context, id + "F40", { "sketchPlane" : qUnion([Q0])});
            skLineSegment(sketch, "E72.0", {"start": v(110, 5) * mm, "end": v(110, -5) * mm});
            skArc(sketch, "E72.1", {"start": v(110, 5) * mm, "mid": v(109.41, 6.41) * mm, "end": v(108, 7) * mm});
            skLineSegment(sketch, "E72.2", {"start": v(101, 7) * mm, "end": v(108, 7) * mm});
            skArc(sketch, "E72.3", {"start": v(108, -7) * mm, "mid": v(109.41, -6.41) * mm, "end": v(110, -5) * mm});
            skLineSegment(sketch, "E72.4", {"start": v(101, -7) * mm, "end": v(108, -7) * mm});
            skLineSegment(sketch, "E73", {"start": v(101, 7) * mm, "end": v(101, -7) * mm});
            skPoint(sketch, "E74.orphan", {"position": v(-18, 7) * mm});
            skPoint(sketch, "E75.orphan", {"position": v(-18, -7) * mm});
            skSolve(sketch);
        }
        {
            var Q0;
            {var subQ22=sQuery(id+"F40.wireOp",EDGE,"E73");Q0=makeQuery(id+"F40.imprint","IMPRINT",FACE,{"disambiguationData":[TD([[makeQuery(id+"F40.imprint","IMPRINT",EDGE,{"derivedFrom":subQ22}),-1.0]])]});}
            cPlane(context, id + "F41", {"entities" : qUnion([Q0]), "cplaneType" : CPlaneType.OFFSET, "offset" : 10 * mm, "width" : 150 * mm, "height" : 150 * mm});
        }
        {
            var Q0;
            Q0=qCreatedBy(id+"F41.planeOp",FACE);
            var sketch = newSketch(context, id + "F42", { "sketchPlane" : qUnion([Q0])});
            skCircle(sketch, "E76", {"center": v(105.2, -0.3) * mm, "radius": 4 * mm});
            skLineSegment(sketch, "E77", {"start": v(101, -7) * mm, "end": v(109.41, 6.41) * mm, "construction": true});
            skSolve(sketch);
        }
        {
            var Q1;
            Q1=makeQuery(id+"F40.imprint","IMPRINT",FACE,{"disambiguationData":[TD([[makeQuery(id+"F40.imprint","IMPRINT",EDGE,{"derivedFrom":sQuery(id+"F40.wireOp",EDGE,"E72.0")}),-1.0]])]});
            var Q2;
            Q2=makeQuery(id+"F42.imprint","IMPRINT",FACE,{"disambiguationData":[TD([[makeQuery(id+"F42.imprint","IMPRINT",EDGE,{"derivedFrom":sQuery(id+"F42.wireOp",EDGE,"E76")}),1.0]])]});
            loft(context, id + "F43", {"operationType" : NewBodyOperationType.ADD, "sheetProfilesArray" : [{ "sheetProfileEntities" : qUnion([Q1]) }, { "sheetProfileEntities" : qUnion([Q2]) }]});
        }
        {
            var Q0;
            Q0=makeQuery(id+"F43.opLoft","CAP_FACE",FACE,{"disambiguationData":[OSD([makeQuery(id+"F42.imprint","IMPRINT",FACE,{"disambiguationData":[TD([[makeQuery(id+"F42.imprint","IMPRINT",EDGE,{"derivedFrom":sQuery(id+"F42.wireOp",EDGE,"E76")}),1.0]])]})])],"isStart":true});
            var sketch = newSketch(context, id + "F44", { "sketchPlane" : qUnion([Q0])});
            skFitSpline(sketch, "E78.0", {"points": [v(106.64, 3.44) * mm, v(106.3, 3.57) * mm, v(105.97, 3.65) * mm, v(105.62, 3.69) * mm, v(105.27, 3.72) * mm, v(104.93, 3.71) * mm, v(104.58, 3.66) * mm, v(104.23, 3.6) * mm, v(103.9, 3.5) * mm, v(103.58, 3.36) * mm, v(103.26, 3.22) * mm, v(102.96, 3.03) * mm, v(102.69, 2.81) * mm]});
            skFitSpline(sketch, "E78.1", {"points": [v(109.16, 0.34) * mm, v(109.1, 0.68) * mm, v(109, 1.02) * mm, v(108.86, 1.34) * mm, v(108.72, 1.66) * mm, v(108.54, 1.95) * mm, v(108.31, 2.23) * mm, v(108.1, 2.5) * mm, v(107.84, 2.74) * mm, v(107.56, 2.95) * mm, v(107.27, 3.15) * mm, v(106.97, 3.32) * mm, v(106.64, 3.44) * mm]});
            skFitSpline(sketch, "E78.2", {"points": [v(107.73, -3.4) * mm, v(108, -3.18) * mm, v(108.24, -2.93) * mm, v(108.45, -2.64) * mm, v(108.65, -2.36) * mm, v(108.82, -2.05) * mm, v(108.94, -1.72) * mm, v(109.07, -1.4) * mm, v(109.15, -1.06) * mm, v(109.19, -0.7) * mm, v(109.22, -0.36) * mm, v(109.21, -0.01) * mm, v(109.16, 0.34) * mm]});
            skFitSpline(sketch, "E78.3", {"points": [v(103.78, -4.03) * mm, v(104.1, -4.15) * mm, v(104.44, -4.23) * mm, v(104.8, -4.27) * mm, v(105.14, -4.3) * mm, v(105.49, -4.3) * mm, v(105.84, -4.24) * mm, v(106.18, -4.19) * mm, v(106.52, -4.09) * mm, v(106.84, -3.95) * mm, v(107.16, -3.8) * mm, v(107.45, -3.62) * mm, v(107.73, -3.4) * mm]});
            skFitSpline(sketch, "E78.4", {"points": [v(101.26, -0.92) * mm, v(101.31, -1.27) * mm, v(101.41, -1.6) * mm, v(101.55, -1.92) * mm, v(101.7, -2.24) * mm, v(101.88, -2.54) * mm, v(102.1, -2.81) * mm, v(102.32, -3.09) * mm, v(102.57, -3.32) * mm, v(102.86, -3.53) * mm, v(103.14, -3.74) * mm, v(103.45, -3.9) * mm, v(103.78, -4.03) * mm]});
            skFitSpline(sketch, "E78.5", {"points": [v(102.69, 2.81) * mm, v(102.41, 2.6) * mm, v(102.18, 2.34) * mm, v(101.97, 2.06) * mm, v(101.76, 1.77) * mm, v(101.6, 1.47) * mm, v(101.47, 1.14) * mm, v(101.35, 0.81) * mm, v(101.27, 0.47) * mm, v(101.23, 0.12) * mm, v(101.2, -0.23) * mm, v(101.2, -0.57) * mm, v(101.26, -0.92) * mm]});
            skSolve(sketch);
        }
        {
            var Q0;
            Q0=makeQuery(id+"F44.imprint","IMPRINT",FACE,{"disambiguationData":[TD([[makeQuery(id+"F44.imprint","IMPRINT",EDGE,{"derivedFrom":sQuery(id+"F44.wireOp",EDGE,"E78.0")}),1.0]])]});
            extrude(context, id + "F45", {"entities" : qUnion([Q0]), "operationType" : NewBodyOperationType.ADD, "depth" : 5 * mm});
        }
        {
            var Q0;
            Q0=makeQuery(id+"F45.opExtrude","CAP_FACE",FACE,{"disambiguationData":[OSD([sQuery(id+"F44.wireOp",EDGE,"E78.0"),sQuery(id+"F44.wireOp",EDGE,"E78.1"),sQuery(id+"F44.wireOp",EDGE,"E78.2"),sQuery(id+"F44.wireOp",EDGE,"E78.3"),sQuery(id+"F44.wireOp",EDGE,"E78.4"),sQuery(id+"F44.wireOp",EDGE,"E78.5")])],"isStart":false});
            var sketch = newSketch(context, id + "F46", { "sketchPlane" : qUnion([Q0])});
            skCircle(sketch, "E79", {"center": v(105.2, -0.3) * mm, "radius": 4 * mm, "construction": true});
            skPoint(sketch, "E80", {"position": v(105.2, 3.7) * mm});
            skLineSegment(sketch, "E81", {"start": v(105.2, -0.3) * mm, "end": v(105.2, 3.7) * mm, "construction": true});
            skSolve(sketch);
        }
        {
            var Q0;
            Q0=makeQuery(id+"F27.opExtrude","SWEPT_FACE",FACE,{"disambiguationData":[OSD([sQuery(id+"F26.wireOp",EDGE,"E60.right")])]});
            var Q1;
            Q1=sQuery(id+"F46.wireOp",VERTEX,"E79.center");
            cPlane(context, id + "F47", {"entities" : qUnion([Q0, Q1]), "cplaneType" : CPlaneType.PLANE_POINT, "offset" : 25 * mm, "width" : 150 * mm, "height" : 150 * mm});
        }
        {
            var Q0;
            Q0=qCreatedBy(id+"F47.planeOp",FACE);
            var sketch = newSketch(context, id + "F48", { "sketchPlane" : qUnion([Q0])});
            skLineSegment(sketch, "E82.bottom", {"start": v(-28, 3.7) * mm, "end": v(-25, 3.7) * mm});
            skLineSegment(sketch, "E82.top", {"start": v(-28, 3.2) * mm, "end": v(-25, 3.2) * mm});
            skLineSegment(sketch, "E82.left", {"start": v(-28, 3.7) * mm, "end": v(-28, 3.2) * mm});
            skLineSegment(sketch, "E82.right", {"start": v(-25, 3.7) * mm, "end": v(-25, 3.2) * mm});
            skSolve(sketch);
        }
        {
            var Q0;
            Q0=makeQuery(id+"F48.imprint","IMPRINT",FACE,{"disambiguationData":[TD([[makeQuery(id+"F48.imprint","IMPRINT",EDGE,{"derivedFrom":sQuery(id+"F48.wireOp",EDGE,"E82.bottom")}),-1.0]])]});
            var Q1;
            Q1=sQuery(id+"F46.wireOp",EDGE,"E79");
            revolve(context, id + "F49", {"operationType" : NewBodyOperationType.REMOVE, "entities" : qUnion([Q0]), "axis" : qUnion([Q1]), "revolveType" : RevolveType.FULL, "oppositeDirection" : true});
        }
        {
            var Q0;
            Q0=makeQuery(id+"F45.opExtrude","CAP_FACE",FACE,{"disambiguationData":[OSD([sQuery(id+"F44.wireOp",EDGE,"E78.0"),sQuery(id+"F44.wireOp",EDGE,"E78.1"),sQuery(id+"F44.wireOp",EDGE,"E78.2"),sQuery(id+"F44.wireOp",EDGE,"E78.3"),sQuery(id+"F44.wireOp",EDGE,"E78.4"),sQuery(id+"F44.wireOp",EDGE,"E78.5")])],"isStart":false});
            var sketch = newSketch(context, id + "F50", { "sketchPlane" : qUnion([Q0])});
            skCircle(sketch, "E83", {"center": v(105.2, -0.3) * mm, "radius": 2 * mm});
            skSolve(sketch);
        }
        {
            var Q0;
            Q0 = qSketchRegion(id + "F50", true);
            extrude(context, id + "F51", {"entities" : qUnion([Q0]), "operationType" : NewBodyOperationType.REMOVE, "endBound" : BoundingType.THROUGH_ALL, "oppositeDirection" : true, "depth" : 25 * mm});
        }
        {
            var Q0;
            Q0=makeQuery(id+"F27.opExtrude","CAP_FACE",FACE,{"disambiguationData":[OSD([sQuery(id+"F26.wireOp",EDGE,"E60.bottom"),sQuery(id+"F26.wireOp",EDGE,"E60.top"),sQuery(id+"F26.wireOp",EDGE,"E60.left"),sQuery(id+"F26.wireOp",EDGE,"E60.right")])],"isStart":true});
            var sketch = newSketch(context, id + "F52", { "sketchPlane" : qUnion([Q0])});
            skCircle(sketch, "E84.0", {"center": v(-105.2, -0.3) * mm, "radius": 2 * mm});
            skSolve(sketch);
        }
        {
            var Q0;
            Q0 = qSketchRegion(id + "F52", true);
            extrude(context, id + "F53", {"entities" : qUnion([Q0]), "operationType" : NewBodyOperationType.REMOVE, "endBound" : BoundingType.THROUGH_ALL, "oppositeDirection" : true, "depth" : 25 * mm});
        }
    });
